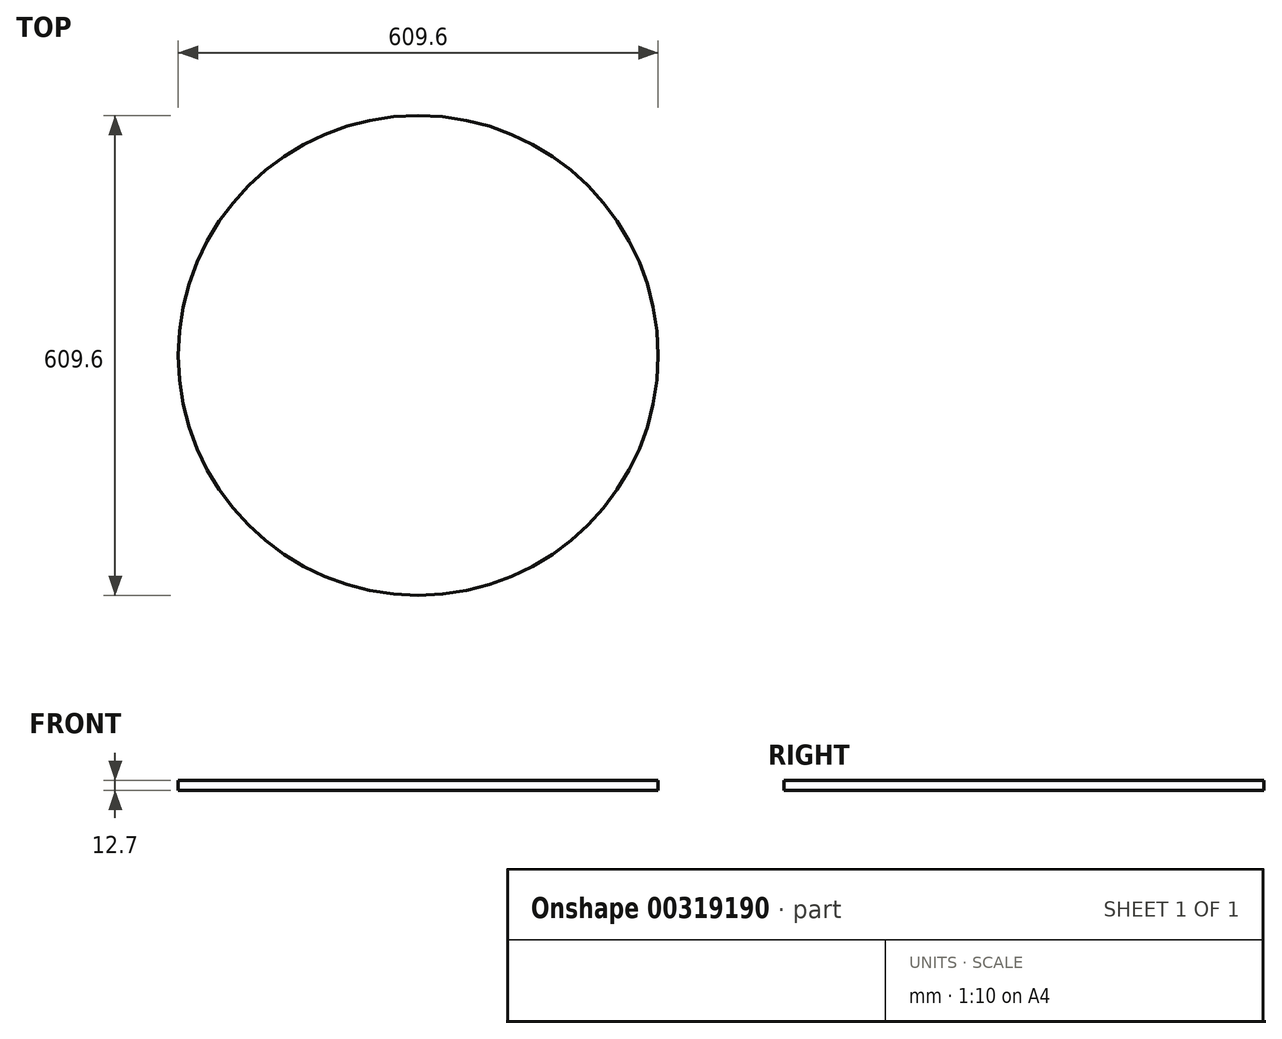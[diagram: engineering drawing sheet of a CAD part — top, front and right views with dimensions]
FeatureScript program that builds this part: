
annotation { "Feature Type Name" : "Feature", "Feature Type Description" : "" }
export const myFeature = defineFeature(function(context is Context, id is Id, definition is map)
    precondition{}
    {
        {
            var Q0;
            Q0=qCreatedBy(makeId("Top.planeOp"),FACE);
            var sketch = newSketch(context, id + "F0", { "sketchPlane" : qUnion([Q0])});
            skCircle(sketch, "E0", {"center": v(0, 0) * mm, "radius": 304.8 * mm});
            skSolve(sketch);
        }
        {
            var Q0;
            Q0=makeQuery(id+"F0.imprint","IMPRINT",FACE,{"disambiguationData":[TD([[makeQuery(id+"F0.imprint","IMPRINT",EDGE,{"derivedFrom":sQuery(id+"F0.wireOp",EDGE,"E0")}),1.0]])]});
            extrude(context, id + "F1", {"entities" : qUnion([Q0]), "depth" : 12.7 * mm});
        }
    });
